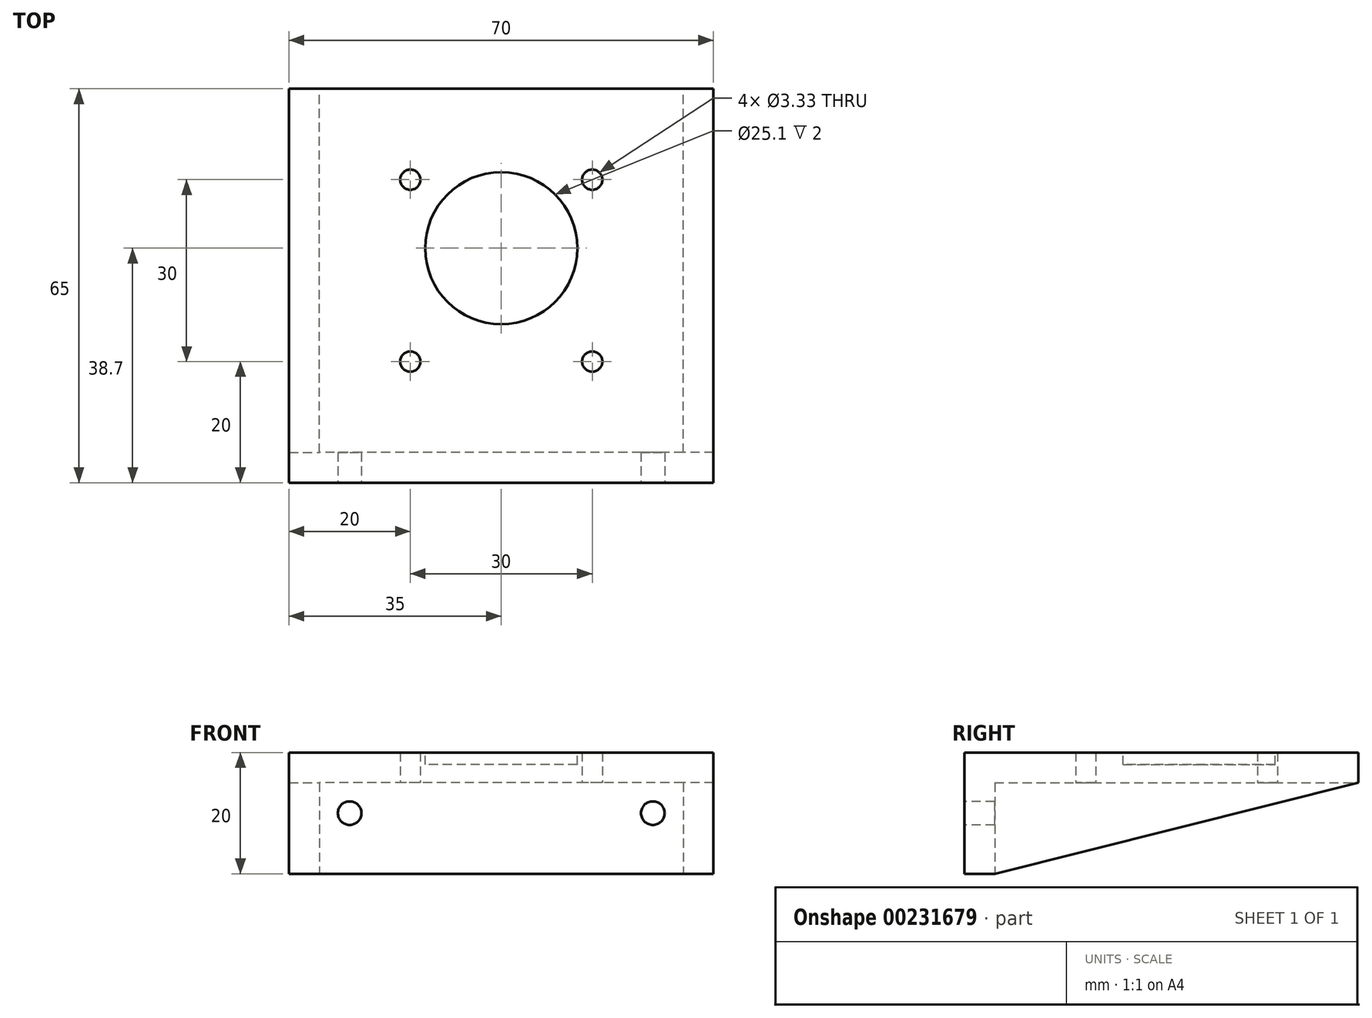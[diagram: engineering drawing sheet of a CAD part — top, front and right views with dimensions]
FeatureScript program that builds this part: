
annotation { "Feature Type Name" : "Feature", "Feature Type Description" : "" }
export const myFeature = defineFeature(function(context is Context, id is Id, definition is map)
    precondition{}
    {
        {
            var Q0;
            Q0=qCreatedBy(makeId("Top.planeOp"),FACE);
            var sketch = newSketch(context, id + "F0", { "sketchPlane" : qUnion([Q0])});
            skLineSegment(sketch, "E0.bottom", {"start": v(30, -30) * mm, "end": v(-30, -30) * mm});
            skLineSegment(sketch, "E0.top", {"start": v(30, 30) * mm, "end": v(-30, 30) * mm});
            skLineSegment(sketch, "E0.left", {"start": v(30, -30) * mm, "end": v(30, 30) * mm});
            skLineSegment(sketch, "E0.right", {"start": v(-30, -30) * mm, "end": v(-30, 30) * mm});
            skPoint(sketch, "E0.middle", {"position": v(0, 0) * mm});
            skLineSegment(sketch, "E1", {"start": v(30, 30) * mm, "end": v(0, 0) * mm, "construction": true});
            skCircle(sketch, "E2", {"center": v(15, 15) * mm, "radius": 1.67 * mm});
            skCircle(sketch, "E3.1.1", {"center": v(-15, 15) * mm, "radius": 1.67 * mm});
            skCircle(sketch, "E3.2.1", {"center": v(-15, -15) * mm, "radius": 1.67 * mm});
            skCircle(sketch, "E3.3.1", {"center": v(15, -15) * mm, "radius": 1.67 * mm});
            skSolve(sketch);
        }
        {
            var Q0;
            Q0 = qSketchRegion(id + "F0", true);
            extrude(context, id + "F1", {"entities" : qUnion([Q0]), "depth" : 5 * mm});
        }
        {
            var Q0;
            Q0=makeQuery(id+"F1.opExtrude","SWEPT_FACE",FACE,{"disambiguationData":[OSD([sQuery(id+"F0.wireOp",EDGE,"E0.bottom")])]});
            var sketch = newSketch(context, id + "F2", { "sketchPlane" : qUnion([Q0])});
            skLineSegment(sketch, "E4.bottom", {"start": v(-30, 5) * mm, "end": v(30, 5) * mm});
            skLineSegment(sketch, "E4.top", {"start": v(-30, -15) * mm, "end": v(30, -15) * mm});
            skLineSegment(sketch, "E4.left", {"start": v(-30, 5) * mm, "end": v(-30, -15) * mm});
            skLineSegment(sketch, "E4.right", {"start": v(30, 5) * mm, "end": v(30, -15) * mm});
            skSolve(sketch);
        }
        {
            var Q0;
            Q0 = qSketchRegion(id + "F2", true);
            extrude(context, id + "F3", {"entities" : qUnion([Q0]), "operationType" : NewBodyOperationType.ADD, "depth" : 5 * mm});
        }
        {
            var Q0;
            Q0=makeQuery(id+"F3.boolean.opBoolean","MERGE",FACE,{"derivedFrom":[makeQuery(id+"F1.opExtrude","SWEPT_FACE",FACE,{"disambiguationData":[OSD([sQuery(id+"F0.wireOp",EDGE,"E0.left")])]}),makeQuery(id+"F3.opExtrude","SWEPT_FACE",FACE,{"disambiguationData":[OSD([sQuery(id+"F2.wireOp",EDGE,"E4.right")])]})]});
            var sketch = newSketch(context, id + "F4", { "sketchPlane" : qUnion([Q0])});
            skLineSegment(sketch, "E5", {"start": v(30, 0) * mm, "end": v(-30, -15) * mm});
            skLineSegment(sketch, "E6", {"start": v(-30, -15) * mm, "end": v(-35, -15) * mm});
            skLineSegment(sketch, "E7", {"start": v(-35, -15) * mm, "end": v(-35, 5) * mm});
            skLineSegment(sketch, "E8", {"start": v(-35, 5) * mm, "end": v(30, 5) * mm});
            skLineSegment(sketch, "E9", {"start": v(30, 5) * mm, "end": v(30, 0) * mm});
            skSolve(sketch);
        }
        {
            var Q0;
            Q0 = qSketchRegion(id + "F4", true);
            extrude(context, id + "F5", {"entities" : qUnion([Q0]), "operationType" : NewBodyOperationType.ADD, "depth" : 5 * mm});
        }
        {
            var Q0;
            Q0=makeQuery(id+"F1.opExtrude","SWEPT_BODY",BODY,{"disambiguationData":[OSD([sQuery(id+"F0.wireOp",EDGE,"E0.bottom"),sQuery(id+"F0.wireOp",EDGE,"E0.top"),sQuery(id+"F0.wireOp",EDGE,"E0.left"),sQuery(id+"F0.wireOp",EDGE,"E0.right"),sQuery(id+"F0.wireOp",EDGE,"E2"),sQuery(id+"F0.wireOp",EDGE,"E3.1.1"),sQuery(id+"F0.wireOp",EDGE,"E3.2.1"),sQuery(id+"F0.wireOp",EDGE,"E3.3.1")])]});
            var Q1;
            Q1=qCreatedBy(makeId("Right.planeOp"),FACE);
            mirror(context, id + "F6", {"operationType" : NewBodyOperationType.ADD, "entities" : qUnion([Q0]), "mirrorPlane" : qUnion([Q1])});
        }
        {
            var Q0;
            {var subQ0=makeQuery(id+"F5.boolean.opBoolean","MERGE",FACE,{"derivedFrom":[makeQuery(id+"F3.opExtrude","CAP_FACE",FACE,{"disambiguationData":[OSD([sQuery(id+"F2.wireOp",EDGE,"E4.bottom"),sQuery(id+"F2.wireOp",EDGE,"E4.top"),sQuery(id+"F2.wireOp",EDGE,"E4.left"),sQuery(id+"F2.wireOp",EDGE,"E4.right")])],"isStart":false}),makeQuery(id+"F5.opExtrude","SWEPT_FACE",FACE,{"disambiguationData":[OSD([sQuery(id+"F4.wireOp",EDGE,"E7")])]})]});Q0=makeQuery(id+"F6.boolean.opBoolean","MERGE",FACE,{"derivedFrom":[subQ0,makeQuery(id+"F6.opPattern","COPY",FACE,{"derivedFrom":subQ0,"instanceName":"1"})]});}
            var sketch = newSketch(context, id + "F7", { "sketchPlane" : qUnion([Q0])});
            skLineSegment(sketch, "E10", {"start": v(-35, -5) * mm, "end": v(35, -5) * mm, "construction": true});
            skLineSegment(sketch, "E11", {"start": v(0, 5) * mm, "end": v(0, -15) * mm, "construction": true});
            skCircle(sketch, "E12", {"center": v(-25, -5) * mm, "radius": 1.95 * mm});
            skCircle(sketch, "E13.MirrorC", {"center": v(25, -5) * mm, "radius": 1.95 * mm});
            skSolve(sketch);
        }
        {
            var Q0;
            Q0 = qSketchRegion(id + "F7", true);
            extrude(context, id + "F8", {"entities" : qUnion([Q0]), "operationType" : NewBodyOperationType.REMOVE, "endBound" : BoundingType.UP_TO_NEXT, "oppositeDirection" : true, "depth" : 25 * mm});
        }
        {
            var Q0;
            {var subQ0=makeQuery(id+"F5.boolean.opBoolean","MERGE",FACE,{"derivedFrom":[makeQuery(id+"F3.boolean.opBoolean","MERGE",FACE,{"derivedFrom":[makeQuery(id+"F1.opExtrude","CAP_FACE",FACE,{"disambiguationData":[OSD([sQuery(id+"F0.wireOp",EDGE,"E0.bottom"),sQuery(id+"F0.wireOp",EDGE,"E0.top"),sQuery(id+"F0.wireOp",EDGE,"E0.left"),sQuery(id+"F0.wireOp",EDGE,"E0.right"),sQuery(id+"F0.wireOp",EDGE,"E2"),sQuery(id+"F0.wireOp",EDGE,"E3.1.1"),sQuery(id+"F0.wireOp",EDGE,"E3.2.1"),sQuery(id+"F0.wireOp",EDGE,"E3.3.1")])],"isStart":false}),makeQuery(id+"F3.opExtrude","SWEPT_FACE",FACE,{"disambiguationData":[OSD([sQuery(id+"F2.wireOp",EDGE,"E4.bottom")])]})]}),makeQuery(id+"F5.opExtrude","SWEPT_FACE",FACE,{"disambiguationData":[OSD([sQuery(id+"F4.wireOp",EDGE,"E8")])]})]});Q0=makeQuery(id+"F6.boolean.opBoolean","MERGE",FACE,{"derivedFrom":[subQ0,makeQuery(id+"F6.opPattern","COPY",FACE,{"derivedFrom":subQ0,"instanceName":"1"})]});}
            var sketch = newSketch(context, id + "F9", { "sketchPlane" : qUnion([Q0])});
            skCircle(sketch, "E14", {"center": v(0, 3.7) * mm, "radius": 12.55 * mm});
            skLineSegment(sketch, "E15", {"start": v(0, 30) * mm, "end": v(0, 16.25) * mm, "construction": true});
            skSolve(sketch);
        }
        {
            var Q0;
            Q0 = qSketchRegion(id + "F9", true);
            extrude(context, id + "F10", {"entities" : qUnion([Q0]), "operationType" : NewBodyOperationType.REMOVE, "oppositeDirection" : true, "depth" : 2 * mm});
        }
    });
